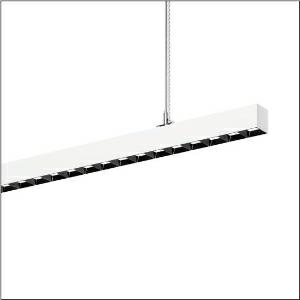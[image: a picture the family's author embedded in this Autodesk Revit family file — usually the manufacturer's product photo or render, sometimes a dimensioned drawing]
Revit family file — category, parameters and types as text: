
# Revit family: silica_21_51mx31tat7w
name_source: partatom
category: Lighting Fixtures
units: mm (PartAtom-declared; Revit-internal decimal feet)

## family parameters
Cut with Voids When Loaded = No
Host = Face
Light Source = No
Part Type = Normal
Room Calculation Point = No
Round Connector Dimension = Use Diameter
Shared = No

## types (1)
- --- (1 x LED, 6220 lm, 53.5 W, 6500K)
    Apparent Load = 54 VA
    CIE Flux Codes = 85 99 100 60 100
    Color Rendering = 80
    Color Temperature = 6500K
    Default Elevation = 1800 mm
    Description = Silica 21, office luminaire, primary light control with darklight reflector, of PMMA, black, CAT 2 (L<= 3000cd/m²), light emission: direct/indirect distribution, primary light characteristic: symmetric, installation type: suspended mounting, LED, rated luminous flux: 6.220lm, luminous efficacy: 111lm/W, light colour: 8tw, colour temperature: 2700..6500K, control gear: DALI DT8, with terminal, 3+2-pole, max. 2.5mm², mains connection: 220..240V, AC, 50/60Hz, rated input power: 56.2W, luminaire housing, of aluminium, traffic white (RAL 9016), length: 1.204mm, width: 53mm, height: 53mm, protection rating (complete): IP20, insulation class (complete): insulation class I (protective earthing), certification: CE, permissible operating ambient temperature: 0..+35°C, standard: EN 50419, packaging unit: 1 piece
    Height = 53 mm
    Lamp = 1 x LED
    Lamp Light Flux = 6220 lm
    Lamp Power = 53.5 W
    Lamp count = 1
    Length = 1204 mm
    Luminous efficacy = 116 lm/W
    Manufacturer = Siteco
    ModVariant = No
    Model = 51MX31TAT7W
    Mounting Place = Ceiling
    Mounting Type = Pendant
    Number of Poles = 1
    OnlyDefault = Yes
    Power Factor = 1
    Product Name = Silica 21
    Product group = office luminaire | ceiling pendant
    ProductGroupID = 903
    Protection Class = Protection class I
    Protection Degree = IP 20
    RLX_Detail_Level = 1
    RLX_Emergency_Light_Flux = 0 lm
    RLX_Emergency_Type = 0
    RLX_Emergency_Type_DB = No
    RlxData = <blob elided: 40493 chars, md5=e2ea1eff>
    Socket = socket
    Standby Power = 0 W
    System Light Flux = 6220 lm
    System Power = 54 W
    Type Comments = individual setting
    Type Image = l_1335871.jpg
    URL = http://relux.com
    VarID = @adj_139403
    Voltage = 0 V
    Weight = 0.00 kg
    Width = 53 mm

## geometry (parser evidence)
native form markers: Blend x4, Sweep x11
no freeform markers — native parametric forms only
